# Revit family: Amplificador de Sinal Endereçável AS2-E ILUMAC
name_source: partatom
category: Dispositivos de alarme de incêndio
units: mm (PartAtom-declared; Revit-internal decimal feet)

## family parameters
Com base no plano de trabalho = Não
Compartilhado = Não
Corte com vazios quando carregada = Não
Cota do conector redondo = Utilizar diâmetro
Manter orientação da anotação = Não
Número OmniClass = 23.80.30.11.17
Ponto de cálculo do ambiente = Não
Sempre na vertical = Sim
Tipo de parte = Normal
Título OmniClass = Distribution Boards and Control Panels

## types (1)
- AS2-E
    Correntes de consumo = 5mA @ 24Vcc
    Código = 002250
    Descrição = Amplificador de Sinal Endereçável AS2-E
    Dimensões (AxLxP) = 60x100x28mm
    Elevação padrão = 0 mm  [stored 0 ft]
    Fabricante = ILUMAC
    Fixação = Caixa de sobrepor com bornes de conexão
    Grau de proteção = IP20 (uso interno)
    Impedância do drive de comunicação = 47K Ohms
    Material da caixa = a Caixa plástica ABS cinza
    Modelo = AS2-E
    Normas técnicas aplicáveis = NBR 17240 | ISO 7240-18
    Peso = 75g
    Protocolo de comunicação = ALF-500 (proprietário)
    Temperatura de operação = 0 à 50oC
    Tensão de operação = 22 à 28Vcc
    Tensão nominal = 24Vcc
    Topologia da rede = Classe B (3 fios)
    Umidade relativa = 0 à 95% (sem condensação)

note: [stored X ft] marks values corroborated as IEEE doubles in the binary element streams (Revit-internal decimal feet)
